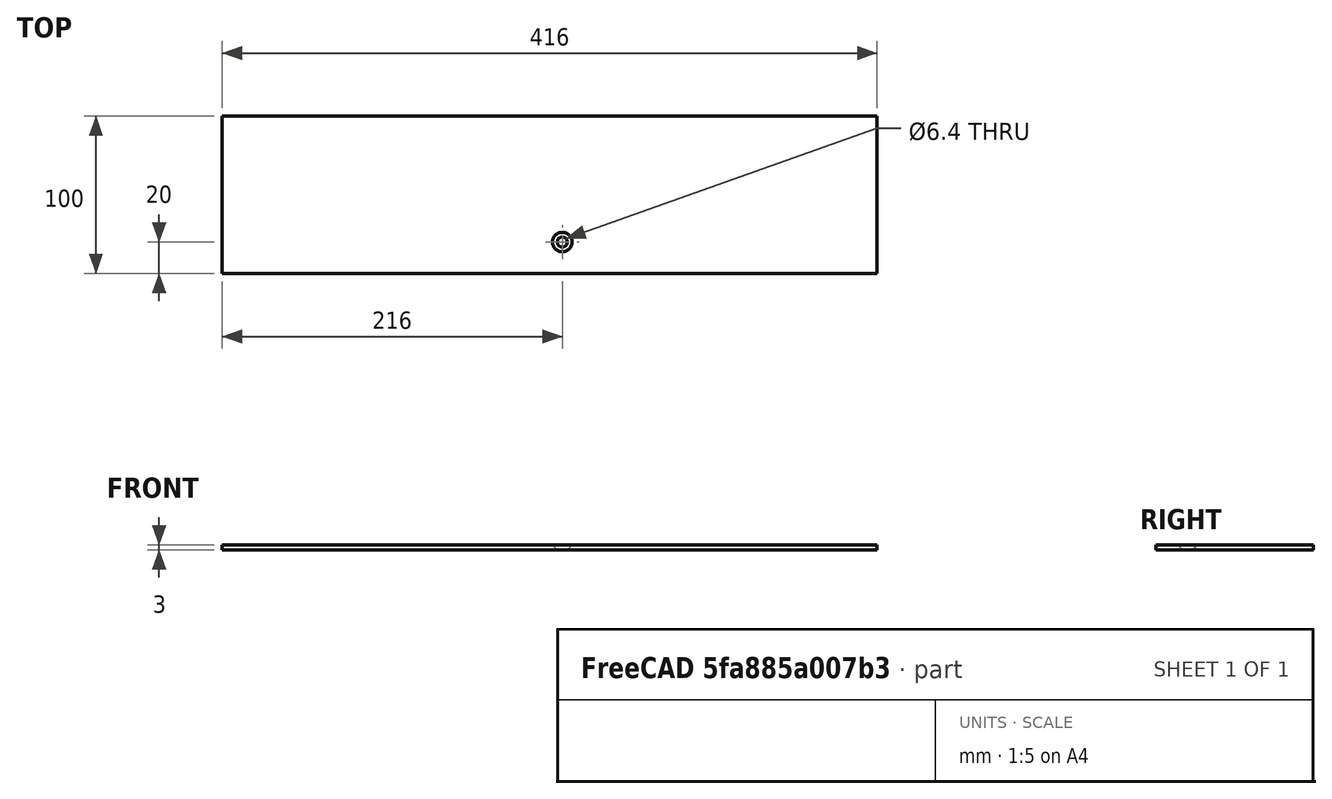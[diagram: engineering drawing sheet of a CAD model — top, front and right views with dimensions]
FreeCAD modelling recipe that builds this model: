
FCSTD DOCUMENT  (FreeCAD 1.0R39319 (Git))
Label: 13_lamella_sheet_knob
License: All rights reserved
LicenseURL: http://en.wikipedia.org/wiki/All_rights_reserved
objects: TechDraw::DrawViewDimension×10, TechDraw::DrawProjGroupItem×4, Sketcher::SketchObject×2, TechDraw::DrawViewAnnotation×2, Spreadsheet::Sheet×1, PartDesign::Pad×1, PartDesign::Pocket×1, PartDesign::Chamfer×1, PartDesign::Body×1, TechDraw::DrawSVGTemplate×1, TechDraw::DrawProjGroup×1, TechDraw::DrawViewBalloon×1, TechDraw::DrawPage×1
note: 27 computed .brp shape members not serialized (recipe doc carries the construction recipe); baked Part::Feature solids carry a one-line shape summary decoded from their .brp

FEATURE [Spreadsheet::Sheet] Spreadsheet
  cells = A4='length; B4(length)=416; A5='width; B5(width)=100; A6='height; B6(height)=3
FEATURE [Sketcher::SketchObject] Sketch
  ArcFitTolerance = 1e-06
  AttachmentSupport = -> [XY_Plane]
  FullyConstrained = true
  MakeInternals = false
  MapMode = 5
  expr: Constraints[11] = Spreadsheet.length
  expr: Constraints[12] = Spreadsheet.width
  sketch-geometry (5):
    g0: LineSegment StartX=-208 StartY=50 StartZ=0 EndX=-208 EndY=-50 EndZ=0
    g1: LineSegment StartX=-208 StartY=-50 StartZ=0 EndX=208 EndY=-50 EndZ=0
    g2: LineSegment StartX=208 StartY=-50 StartZ=0 EndX=208 EndY=50 EndZ=0
    g3: LineSegment StartX=208 StartY=50 StartZ=0 EndX=-208 EndY=50 EndZ=0
    g4: LineSegment [constr] StartX=-208 StartY=50 StartZ=0 EndX=208 EndY=-50 EndZ=0
  constraints (13):
    c: Coincident(g0,g1)
    c: Coincident(g1,g2)
    c: Coincident(g2,g3)
    c: Coincident(g3,g0)
    c: Vertical(g0)
    c: Vertical(g2)
    c: Horizontal(g1)
    c: Horizontal(g3)
    c: Coincident(g4,g0)
    c: Coincident(g4,g1)
    c: Symmetric(g4,g4,g-1)
    c: DistanceX(g3,g3) = 416
    c: DistanceY(g0,g0) = 100
FEATURE [PartDesign::Pad] Pad
  Direction = (0,0,1)
  Length = 3
  Length2 = 10
  Midplane = true
  Profile = -> Sketch
  ReferenceAxis = -> Sketch [N_Axis]
  Suppressed = false
  Type = 0
  expr: Length = Spreadsheet.height
FEATURE [Sketcher::SketchObject] Sketch001
  ArcFitTolerance = 1e-06
  AttachmentSupport = -> [XY_Plane]
  ExternalGeometry = -> [Pad]
  FullyConstrained = true
  MakeInternals = false
  MapMode = 5
  sketch-geometry (2):
    g0: LineSegment [constr] StartX=-208 StartY=-30 StartZ=0 EndX=208 EndY=-30 EndZ=0
    g1: Circle CenterX=8 CenterY=-30 CenterZ=0 NormalX=0 NormalY=0 NormalZ=1 AngleXU=0 Radius=3.2
  constraints (7):
    c: PointOnObject(g0,g-5)
    c: PointOnObject(g0,g-4)
    c: Horizontal(g0)
    c: PointOnObject(g1,g0)
    c: Diameter(g1) = 6.4
    c: DistanceX(g1,g0) = 200
    c: Distance(g0,g-6) = 20
FEATURE [PartDesign::Pocket] Pocket
  BaseFeature = -> Pad
  Direction = (0,0,-1)
  Length = 3
  Length2 = 5
  Midplane = true
  Profile = -> Sketch001
  ReferenceAxis = -> Sketch001 [N_Axis]
  Suppressed = false
  Type = 0
FEATURE [PartDesign::Chamfer] Chamfer
  Angle = 45
  Base = -> Pocket [Edge14]
  BaseFeature = -> Pocket
  ChamferType = 0
  FlipDirection = false
  Size = 2.99
  Size2 = 1
  SupportTransform = false
  Suppressed = false
  UseAllEdges = false
FEATURE [PartDesign::Body] Body
  AllowCompound = false
  Group = -> [Sketch,Pad,Sketch001,Pocket,Chamfer]
  Origin = -> Origin
  Tip = -> Chamfer
FEATURE [TechDraw::DrawSVGTemplate] Template
  EditableTexts = AuthorName=Matthias Mosimann; CheckDate=N/A; CreationDate=11/04/2026; DrawingNumber=1.0; FC-Title=Lamelle; SheetNumber=1 / 1; SupervisorName=N/A; Weight=N/A; scale=1 : 2
  Height = 297
  Orientation = 1
  Template = C:/Program Files/FreeCAD 1.0/data/Mod/TechDraw/Templates/A3_Landscape_TD.svg
  Width = 420
FEATURE [TechDraw::DrawProjGroupItem] View  label="Front"
  CoarseView = false
  Direction = (0,-1,0)
  Focus = 100
  HardHidden = false
  IsoCount = 0
  IsoHidden = false
  IsoVisible = false
  LockPosition = true
  Perspective = false
  Rotation = 0
  RotationVector = (1,0,0)
  Scale = 0.5
  ScaleType = 2
  ScrubCount = 1
  SeamHidden = false
  SeamVisible = true
  SmoothHidden = false
  SmoothVisible = true
  Source = -> [Body]
  Type = 0
  X = 0
  XDirection = (1,0,0)
  Y = 0
FEATURE [TechDraw::DrawProjGroupItem] ProjItem  label="Right"
  CoarseView = false
  Direction = (1,-1e-16,0)
  Focus = 100
  HardHidden = false
  IsoCount = 0
  IsoHidden = false
  IsoVisible = false
  LockPosition = true
  Perspective = false
  Rotation = 0
  RotationVector = (1,0,0)
  ScaleType = 0
  ScrubCount = 1
  SeamHidden = false
  SeamVisible = true
  SmoothHidden = false
  SmoothVisible = true
  Source = -> [Body]
  Type = 2
  X = -137.609
  XDirection = (1e-16,1,0)
  Y = 0
FEATURE [TechDraw::DrawProjGroupItem] ProjItem001  label="Bottom"
  CoarseView = false
  Direction = (0,0,-1)
  Focus = 100
  HardHidden = false
  IsoCount = 0
  IsoHidden = false
  IsoVisible = false
  LockPosition = true
  Perspective = false
  Rotation = 0
  RotationVector = (1,0,0)
  ScaleType = 0
  ScrubCount = 1
  SeamHidden = false
  SeamVisible = true
  SmoothHidden = false
  SmoothVisible = true
  Source = -> [Body]
  Type = 5
  X = 0
  XDirection = (1,0,0)
  Y = 55.2638
FEATURE [TechDraw::DrawProjGroupItem] ProjItem002  label="Top"
  CoarseView = false
  Direction = (0,0,1)
  Focus = 100
  HardHidden = false
  IsoCount = 0
  IsoHidden = false
  IsoVisible = false
  LockPosition = true
  Perspective = false
  Rotation = 0
  RotationVector = (1,0,0)
  ScaleType = 0
  ScrubCount = 1
  SeamHidden = false
  SeamVisible = true
  SmoothHidden = false
  SmoothVisible = true
  Source = -> [Body]
  Type = 4
  X = 0
  XDirection = (1,0,0)
  Y = -53.3386
FEATURE [TechDraw::DrawProjGroup] ProjGroup
  Anchor = -> View
  AutoDistribute = true
  LockPosition = false
  ProjectionType = 0
  Rotation = 0
  Scale = 0.5
  ScaleType = 2
  Source = -> [Body]
  Views = -> [View,ProjItem,ProjItem001,ProjItem002]
  X = 174.51
  Y = 180.101
  spacingX = 30
  spacingY = 30
FEATURE [TechDraw::DrawViewAnnotation] Annotation005
  Font = osifont
  LineSpace = 80
  LockPosition = false
  MaxWidth = 120
  Rotation = 0
  Scale = 0.5
  ScaleType = 1
  Text = Teil wird aus standard Stahlblech hergestellt 3mm. Achtung! Bohrung nur auf einer Lamelle ausführen, für die Befestigung Griff. Alle Angaben in mm. 3D Ansichten können von der angegebenen Skalierungsgrösse abweichen.
  TextSize = 3
  TextStyle = 1
  X = 345.531
  Y = 249.289
FEATURE [TechDraw::DrawViewDimension] Dimension
  AngleOverride = false
  Arbitrary = false
  ArbitraryTolerances = false
  BoxCorners = (2) [(-104,-25,0),(104,25,0)]
  EqualTolerance = true
  ExtensionAngle = 0
  FormatSpec = %.2w
  FormatSpecOverTolerance = %+.2w
  FormatSpecUnderTolerance = %+.2w
  Inverted = false
  LineAngle = 0
  LockPosition = false
  MeasureType = 1
  OverTolerance = 0
  References2D = -> [ProjItem002]
  Rotation = 0
  ScaleType = 0
  TheoreticalExact = false
  Type = 1
  UnderTolerance = 0
  X = 0
  Y = 38.7915
FEATURE [TechDraw::DrawViewDimension] Dimension001
  AngleOverride = false
  Arbitrary = false
  ArbitraryTolerances = false
  BoxCorners = (2) [(-104,-25,0),(104,25,0)]
  EqualTolerance = true
  ExtensionAngle = 0
  FormatSpec = %.2w
  FormatSpecOverTolerance = %+.2w
  FormatSpecUnderTolerance = %+.2w
  Inverted = false
  LineAngle = 0
  LockPosition = false
  MeasureType = 1
  OverTolerance = 0
  References2D = -> [ProjItem002]
  Rotation = 0
  ScaleType = 0
  TheoreticalExact = false
  Type = 2
  UnderTolerance = 0
  X = -130.5
  Y = -4.06414
FEATURE [TechDraw::DrawViewDimension] Dimension002
  AngleOverride = false
  Arbitrary = false
  ArbitraryTolerances = false
  BoxCorners = (2) [(-104,-25,0),(104,25,0)]
  EqualTolerance = true
  ExtensionAngle = 0
  FormatSpec = ⌀%.2w
  FormatSpecOverTolerance = %+.2w
  FormatSpecUnderTolerance = %+.2w
  Inverted = false
  LineAngle = 0
  LockPosition = false
  MeasureType = 1
  OverTolerance = 0
  References2D = -> [ProjItem002]
  Rotation = 0
  ScaleType = 0
  TheoreticalExact = false
  Type = 5
  UnderTolerance = 0
  X = 36.5565
  Y = -37.6341
FEATURE [TechDraw::DrawViewDimension] Dimension003
  AngleOverride = false
  Arbitrary = false
  ArbitraryTolerances = false
  BoxCorners = (2) [(-104,-25,0),(104,25,0)]
  EqualTolerance = true
  ExtensionAngle = 0
  FormatSpec = ⌀%.2w
  FormatSpecOverTolerance = %+.2w
  FormatSpecUnderTolerance = %+.2w
  Inverted = false
  LineAngle = 0
  LockPosition = false
  MeasureType = 1
  OverTolerance = 0
  References2D = -> [ProjItem002]
  Rotation = 0
  ScaleType = 0
  TheoreticalExact = false
  Type = 5
  UnderTolerance = 0
  X = 47.1517
  Y = -29.3846
FEATURE [TechDraw::DrawViewDimension] Dimension004
  AngleOverride = false
  Arbitrary = false
  ArbitraryTolerances = false
  BoxCorners = (2) [(-25,-0.75,0),(25,0.75,0)]
  EqualTolerance = true
  ExtensionAngle = 0
  FormatSpec = %.2w
  FormatSpecOverTolerance = %+.2w
  FormatSpecUnderTolerance = %+.2w
  Inverted = false
  LineAngle = 0
  LockPosition = false
  MeasureType = 1
  OverTolerance = 0
  References2D = -> [ProjItem]
  Rotation = 0
  ScaleType = 0
  TheoreticalExact = false
  Type = 1
  UnderTolerance = 0
  X = 0
  Y = 19.9929
FEATURE [TechDraw::DrawViewDimension] Dimension005
  AngleOverride = false
  Arbitrary = false
  ArbitraryTolerances = false
  BoxCorners = (2) [(-25,-0.75,0),(25,0.75,0)]
  EqualTolerance = true
  ExtensionAngle = 0
  FormatSpec = %.2w
  FormatSpecOverTolerance = %+.2w
  FormatSpecUnderTolerance = %+.2w
  Inverted = false
  LineAngle = 0
  LockPosition = false
  MeasureType = 1
  OverTolerance = 0
  References2D = -> [ProjItem]
  Rotation = 0
  ScaleType = 0
  TheoreticalExact = false
  Type = 0
  UnderTolerance = 0
  X = 21.5226
  Y = -13.0668
FEATURE [TechDraw::DrawViewDimension] Dimension006
  AngleOverride = false
  Arbitrary = false
  ArbitraryTolerances = false
  BoxCorners = (2) [(-104,-25,0),(104,25,0)]
  EqualTolerance = true
  ExtensionAngle = 0
  FormatSpec = %.2w
  FormatSpecOverTolerance = %+.2w
  FormatSpecUnderTolerance = %+.2w
  Inverted = false
  LineAngle = 0
  LockPosition = false
  MeasureType = 1
  OverTolerance = 0
  References2D = -> [ProjItem002]
  Rotation = 0
  ScaleType = 0
  TheoreticalExact = false
  Type = 0
  UnderTolerance = 0
  X = -40.0669
  Y = -45.0862
FEATURE [TechDraw::DrawViewDimension] Dimension007
  AngleOverride = false
  Arbitrary = false
  ArbitraryTolerances = false
  BoxCorners = (2) [(-104,-25,0),(104,25,0)]
  EqualTolerance = true
  ExtensionAngle = 0
  FormatSpec = %.2w
  FormatSpecOverTolerance = %+.2w
  FormatSpecUnderTolerance = %+.2w
  Inverted = false
  LineAngle = 0
  LockPosition = false
  MeasureType = 1
  OverTolerance = 0
  References2D = -> [ProjItem002]
  Rotation = 0
  ScaleType = 0
  TheoreticalExact = false
  Type = 2
  UnderTolerance = 0
  X = 110.73
  Y = -3.0269
FEATURE [TechDraw::DrawViewDimension] Dimension008
  AngleOverride = false
  Arbitrary = false
  ArbitraryTolerances = false
  BoxCorners = (2) [(-104,-25,0),(104,25,0)]
  EqualTolerance = true
  ExtensionAngle = 0
  FormatSpec = %.2w
  FormatSpecOverTolerance = %+.2w
  FormatSpecUnderTolerance = %+.2w
  Inverted = false
  LineAngle = 0
  LockPosition = false
  MeasureType = 1
  OverTolerance = 0
  References2D = -> [ProjItem002]
  Rotation = 0
  ScaleType = 0
  TheoreticalExact = false
  Type = 0
  UnderTolerance = 0
  X = 58.0843
  Y = -45.0862
FEATURE [TechDraw::DrawViewDimension] Dimension009
  AngleOverride = false
  Arbitrary = false
  ArbitraryTolerances = false
  BoxCorners = (2) [(-104,-25,0),(104,25,0)]
  EqualTolerance = true
  ExtensionAngle = 0
  FormatSpec = %.2w
  FormatSpecOverTolerance = %+.2w
  FormatSpecUnderTolerance = %+.2w
  Inverted = false
  LineAngle = 0
  LockPosition = false
  MeasureType = 1
  OverTolerance = 0
  References2D = -> [ProjItem002]
  Rotation = 0
  ScaleType = 0
  TheoreticalExact = false
  Type = 0
  UnderTolerance = 0
  X = -118.92
  Y = -7.95087
FEATURE [TechDraw::DrawViewAnnotation] Annotation
  Font = osifont
  LineSpace = 80
  LockPosition = false
  MaxWidth = 120
  Rotation = 0
  Scale = 0.75
  ScaleType = 1
  Text = (1) Durchgangsloch fein und Senkung für M6. Bitte Bohrung nur für 1 Lamelle ausführen. Die anderen haben keine Griffe!
  TextSize = 3
  TextStyle = 0
  X = 345.531
  Y = 211.752
FEATURE [TechDraw::DrawViewBalloon] Balloon
  BubbleShape = 0
  EndType = 0
  EndTypeScale = 1
  KinkLength = 5
  LockPosition = false
  OriginX = 4.8
  OriginY = -30
  Rotation = 0
  ScaleType = 0
  ShapeScale = 1
  SourceView = -> ProjItem002
  Text = 1
  TextWrapLen = -1
  X = -50.9272
  Y = -121.959
FEATURE [TechDraw::DrawPage] Page
  KeepUpdated = true
  NextBalloonIndex = 2
  ProjectionType = 0
  Template = -> Template
  Views = -> [ProjGroup,Annotation005,Dimension,Dimension001,Dimension002,Dimension003,Dimension004,Dimension005,Dimension006,Dimension007,Dimension008,Dimension009,Annotation,Balloon]
